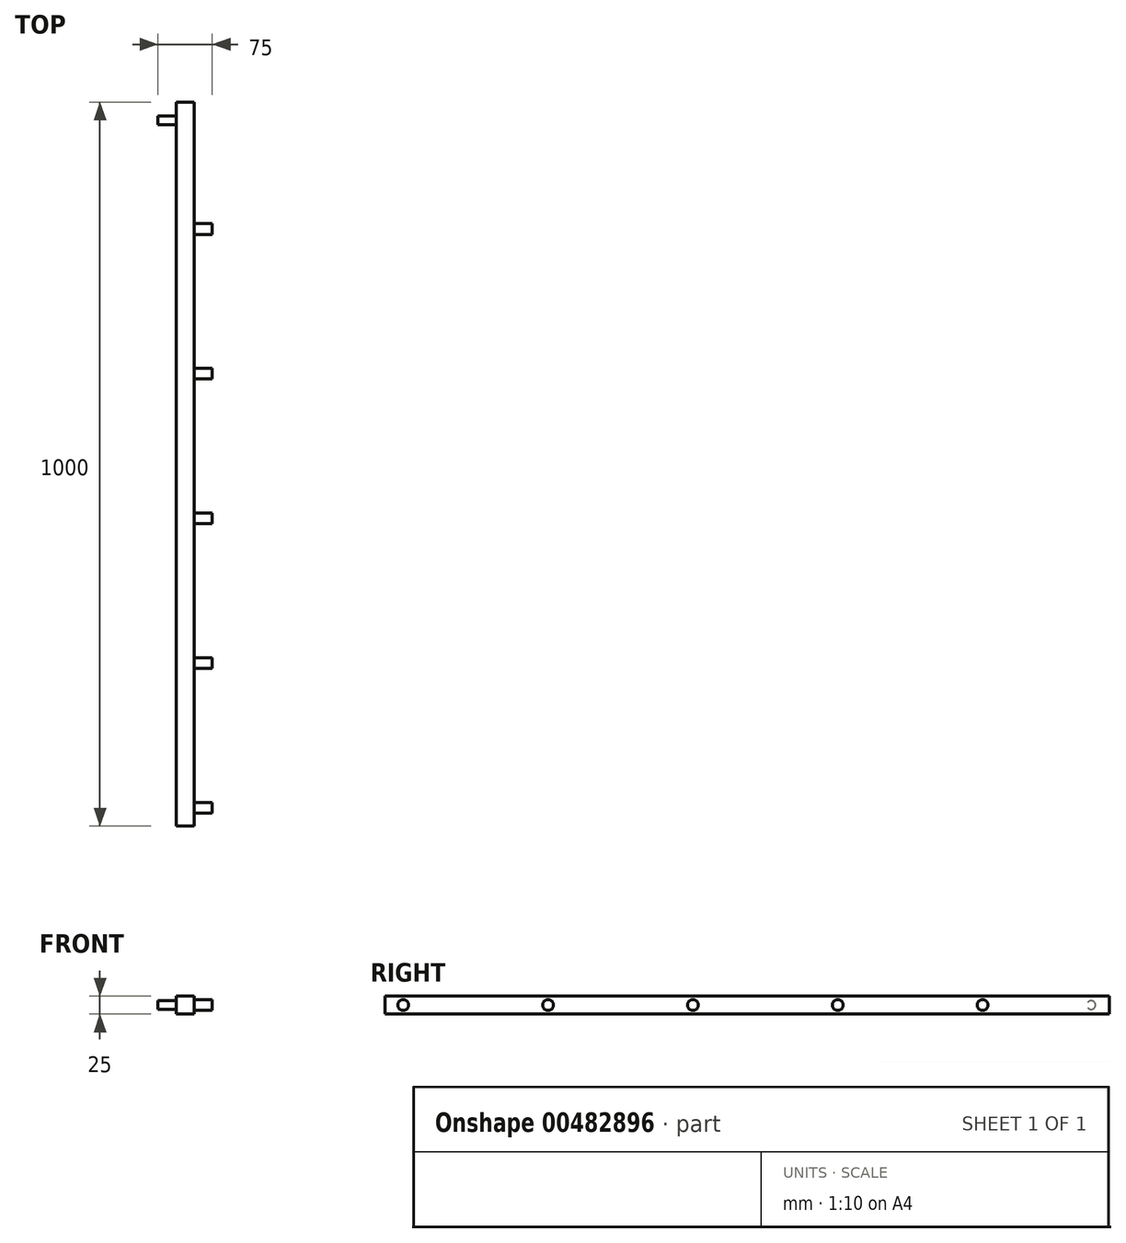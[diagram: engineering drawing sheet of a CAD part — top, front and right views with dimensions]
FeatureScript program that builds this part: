
annotation { "Feature Type Name" : "Feature", "Feature Type Description" : "" }
export const myFeature = defineFeature(function(context is Context, id is Id, definition is map)
    precondition{}
    {
        {
            var Q0;
            Q0=qCreatedBy(makeId("Right.planeOp"),FACE);
            var sketch = newSketch(context, id + "F0", { "sketchPlane" : qUnion([Q0])});
            skLineSegment(sketch, "E0.bottom", {"start": v(500, -12.5) * mm, "end": v(-500, -12.5) * mm});
            skLineSegment(sketch, "E0.top", {"start": v(500, 12.5) * mm, "end": v(-500, 12.5) * mm});
            skLineSegment(sketch, "E0.left", {"start": v(500, -12.5) * mm, "end": v(500, 12.5) * mm});
            skLineSegment(sketch, "E0.right", {"start": v(-500, -12.5) * mm, "end": v(-500, 12.5) * mm});
            skPoint(sketch, "E0.middle", {"position": v(0, 0) * mm});
            skSolve(sketch);
        }
        {
            var Q0;
            Q0=makeQuery(id+"F0.imprint","IMPRINT",FACE,{"disambiguationData":[TD([[makeQuery(id+"F0.imprint","IMPRINT",EDGE,{"derivedFrom":sQuery(id+"F0.wireOp",EDGE,"E0.bottom")}),-1.0]])]});
            extrude(context, id + "F1", {"entities" : qUnion([Q0]), "depth" : 25 * mm});
        }
        {
            var Q0;
            Q0=makeQuery(id+"F1.opExtrude","CAP_FACE",FACE,{"disambiguationData":[OSD([sQuery(id+"F0.wireOp",EDGE,"E0.bottom"),sQuery(id+"F0.wireOp",EDGE,"E0.top"),sQuery(id+"F0.wireOp",EDGE,"E0.left"),sQuery(id+"F0.wireOp",EDGE,"E0.right")])],"isStart":false});
            var sketch = newSketch(context, id + "F2", { "sketchPlane" : qUnion([Q0])});
            skCircle(sketch, "E1", {"center": v(-475, 0) * mm, "radius": 7.5 * mm});
            skCircle(sketch, "E2.1.0.0", {"center": v(-275, 0) * mm, "radius": 7.5 * mm});
            skCircle(sketch, "E2.2.0.0", {"center": v(-75, 0) * mm, "radius": 7.5 * mm});
            skCircle(sketch, "E2.3.0.0", {"center": v(125, 0) * mm, "radius": 7.5 * mm});
            skCircle(sketch, "E2.4.0.0", {"center": v(325, 0) * mm, "radius": 7.5 * mm});
            skLineSegment(sketch, "E2.direction1", {"start": v(-475, 0) * mm, "end": v(-275, 0) * mm, "construction": true});
            skSolve(sketch);
        }
        {
            var Q0;
            Q0=makeQuery(id+"F2.imprint","IMPRINT",FACE,{"disambiguationData":[TD([[makeQuery(id+"F2.imprint","IMPRINT",EDGE,{"derivedFrom":sQuery(id+"F2.wireOp",EDGE,"E1")}),1.0]])]});
            var Q1;
            Q1=makeQuery(id+"F2.imprint","IMPRINT",FACE,{"disambiguationData":[TD([[makeQuery(id+"F2.imprint","IMPRINT",EDGE,{"derivedFrom":sQuery(id+"F2.wireOp",EDGE,"E2.1.0.0")}),1.0]])]});
            var Q2;
            Q2=makeQuery(id+"F2.imprint","IMPRINT",FACE,{"disambiguationData":[TD([[makeQuery(id+"F2.imprint","IMPRINT",EDGE,{"derivedFrom":sQuery(id+"F2.wireOp",EDGE,"E2.2.0.0")}),1.0]])]});
            var Q3;
            Q3=makeQuery(id+"F2.imprint","IMPRINT",FACE,{"disambiguationData":[TD([[makeQuery(id+"F2.imprint","IMPRINT",EDGE,{"derivedFrom":sQuery(id+"F2.wireOp",EDGE,"E2.3.0.0")}),1.0]])]});
            var Q4;
            Q4=makeQuery(id+"F2.imprint","IMPRINT",FACE,{"disambiguationData":[TD([[makeQuery(id+"F2.imprint","IMPRINT",EDGE,{"derivedFrom":sQuery(id+"F2.wireOp",EDGE,"E2.4.0.0")}),1.0]])]});
            extrude(context, id + "F3", {"entities" : qUnion([Q0, Q1, Q2, Q3, Q4]), "operationType" : NewBodyOperationType.ADD, "depth" : 25 * mm});
        }
        {
            var Q0;
            Q0=makeQuery(id+"F1.opExtrude","CAP_FACE",FACE,{"disambiguationData":[OSD([sQuery(id+"F0.wireOp",EDGE,"E0.bottom"),sQuery(id+"F0.wireOp",EDGE,"E0.top"),sQuery(id+"F0.wireOp",EDGE,"E0.left"),sQuery(id+"F0.wireOp",EDGE,"E0.right")])],"isStart":true});
            var sketch = newSketch(context, id + "F4", { "sketchPlane" : qUnion([Q0])});
            skCircle(sketch, "E3", {"center": v(-475, 0) * mm, "radius": 6 * mm});
            skPoint(sketch, "E3.centerSnap0", {"position": v(-500, 0) * mm});
            skSolve(sketch);
        }
        {
            var Q0;
            Q0=makeQuery(id+"F4.imprint","IMPRINT",FACE,{"disambiguationData":[TD([[makeQuery(id+"F4.imprint","IMPRINT",EDGE,{"derivedFrom":sQuery(id+"F4.wireOp",EDGE,"E3")}),1.0]])]});
            extrude(context, id + "F5", {"entities" : qUnion([Q0]), "operationType" : NewBodyOperationType.ADD, "depth" : 25 * mm});
        }
    });
